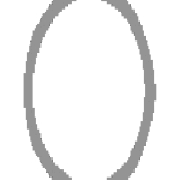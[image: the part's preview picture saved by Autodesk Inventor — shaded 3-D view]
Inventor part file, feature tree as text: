
AUTODESK INVENTOR PART (.ipt)
format: ipt  version: 2021 (Build 250183000, 183)  size: 110,080 bytes
history: native  units: in
note: dims shown in document units (in); Inventor stores cm internally (conversion verified against a paired STEP export)
features: other x4, sketch x3, plane x1
ambient origin geometry x8: Origin, YZ Plane, XZ Plane, XY Plane, X Axis, Y Axis, Z Axis, Center Point
bodies: Solid1 (feature_tree), Body (feature_tree)
feature tree (8):
  other  "Driven Length"
  other  "Frame Generator"
  other  "Start Plane"
  other  "End Plane"
  sketch  "Sketch"  dims[d2=14.4375in d4=-0.0in d5=14.4375in d6=0.12in d7=0.0in d8=90.0deg d9=14.4375in]
  sketch  "Sketch2"  dims[d0=1.0in]
  plane  "Work Plane3"
  sketch  "Sketch3"  dims[d1=0.065in]
